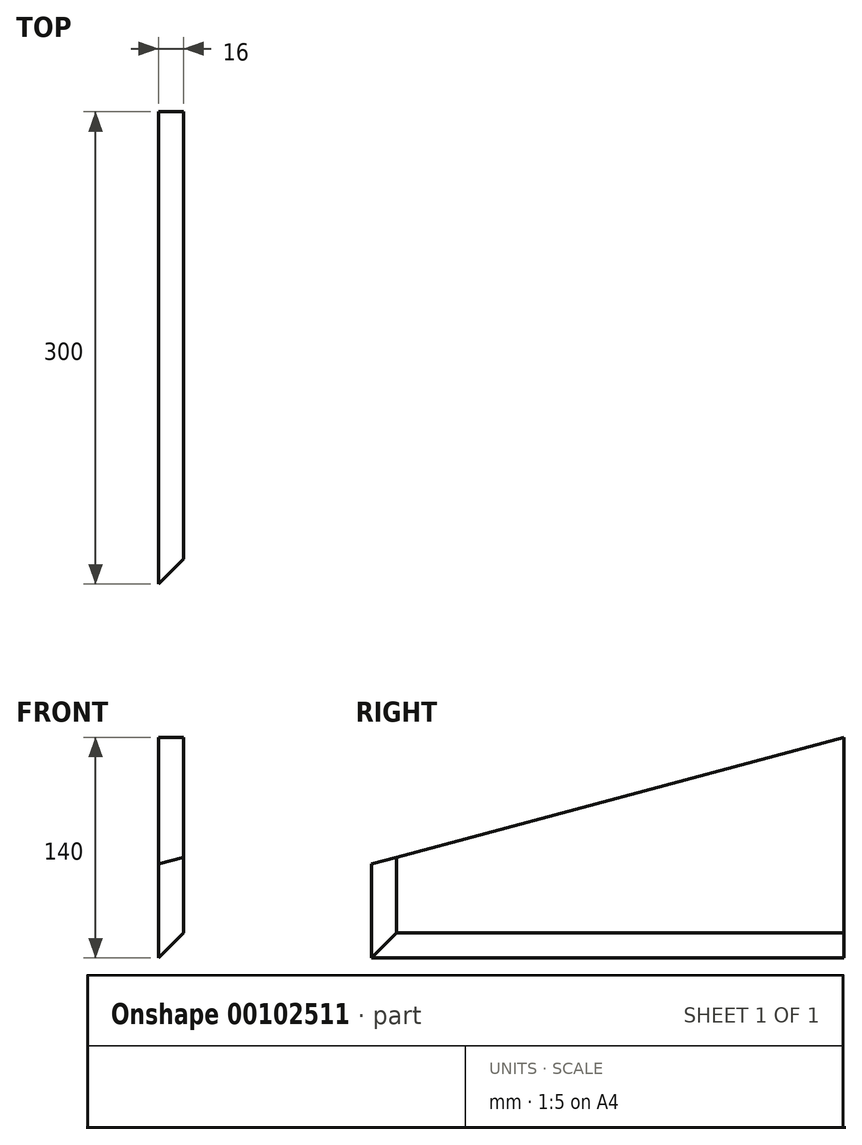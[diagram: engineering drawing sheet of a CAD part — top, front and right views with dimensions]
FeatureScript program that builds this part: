
annotation { "Feature Type Name" : "Feature", "Feature Type Description" : "" }
export const myFeature = defineFeature(function(context is Context, id is Id, definition is map)
    precondition{}
    {
        {
            var Q0;
            Q0=qCreatedBy(makeId("Right.planeOp"),FACE);
            var sketch = newSketch(context, id + "F0", { "sketchPlane" : qUnion([Q0])});
            skLineSegment(sketch, "E0", {"start": v(0, 0) * mm, "end": v(300, 0) * mm});
            skLineSegment(sketch, "E1", {"start": v(300, 0) * mm, "end": v(300, 140) * mm});
            skLineSegment(sketch, "E2", {"start": v(300, 140) * mm, "end": v(0, 59.62) * mm});
            skLineSegment(sketch, "E3", {"start": v(0, 59.62) * mm, "end": v(0, 0) * mm});
            skSolve(sketch);
        }
        {
            var Q0;
            Q0=qSketchRegion(id+"F0",true);
            extrude(context, id + "F1", {"entities" : qUnion([Q0]), "depth" : 16 * mm});
        }
        {
            var Q0;
            Q0=makeQuery(id+"F1.opExtrude","CAP_EDGE",EDGE,{"disambiguationData":[OSD([sQuery(id+"F0.wireOp",EDGE,"E0")])],"isStart":false});
            var Q1;
            Q1=makeQuery(id+"F1.opExtrude","CAP_EDGE",EDGE,{"disambiguationData":[OSD([sQuery(id+"F0.wireOp",EDGE,"E3")])],"isStart":false});
            chamfer(context, id + "F2", {"entities" : qUnion([Q0, Q1]), "width" : 16 * mm, "tangentPropagation" : true});
        }
    });
